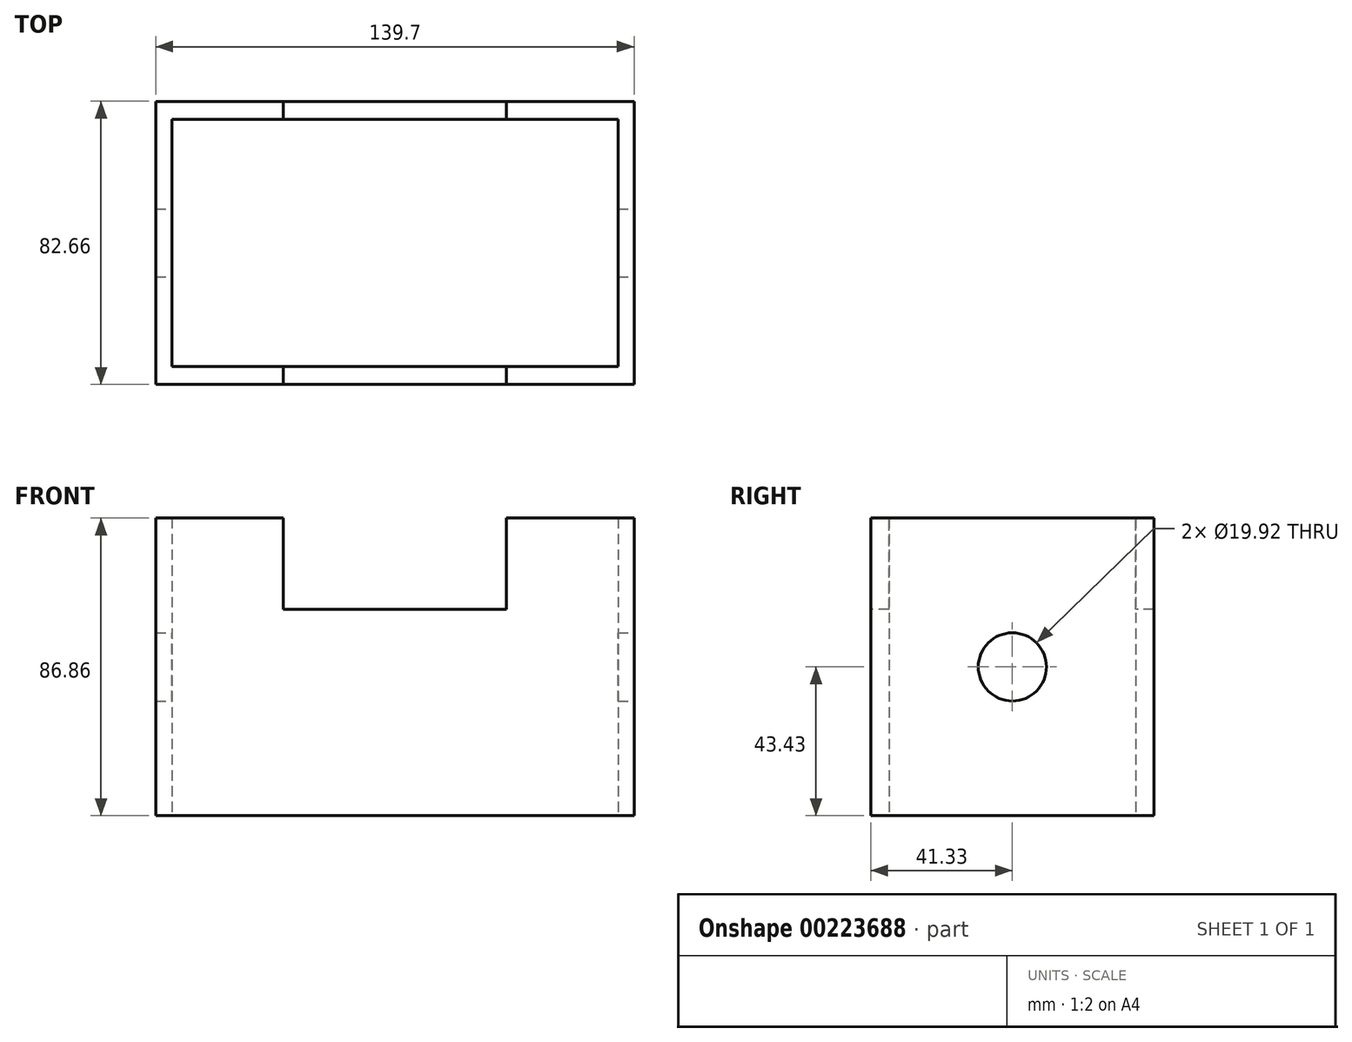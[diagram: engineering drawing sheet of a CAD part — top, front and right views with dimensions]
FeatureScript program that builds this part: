
annotation { "Feature Type Name" : "Feature", "Feature Type Description" : "" }
export const myFeature = defineFeature(function(context is Context, id is Id, definition is map)
    precondition{}
    {
        {
            var Q0;
            Q0=qCreatedBy(makeId("Top.planeOp"),FACE);
            var sketch = newSketch(context, id + "F0", { "sketchPlane" : qUnion([Q0])});
            skLineSegment(sketch, "E0.bottom", {"start": v(69.85, 41.33) * mm, "end": v(-69.85, 41.33) * mm});
            skLineSegment(sketch, "E0.top", {"start": v(69.85, -41.33) * mm, "end": v(-69.85, -41.33) * mm});
            skLineSegment(sketch, "E0.left", {"start": v(69.85, 41.33) * mm, "end": v(69.85, -41.33) * mm});
            skLineSegment(sketch, "E0.right", {"start": v(-69.85, 41.33) * mm, "end": v(-69.85, -41.33) * mm});
            skPoint(sketch, "E0.middle", {"position": v(0, 0) * mm});
            skLineSegment(sketch, "E1.bottom", {"start": v(65.12, 36.04) * mm, "end": v(-65.12, 36.04) * mm});
            skLineSegment(sketch, "E1.top", {"start": v(65.12, -36.04) * mm, "end": v(-65.12, -36.04) * mm});
            skLineSegment(sketch, "E1.left", {"start": v(65.12, 36.04) * mm, "end": v(65.12, -36.04) * mm});
            skLineSegment(sketch, "E1.right", {"start": v(-65.12, 36.04) * mm, "end": v(-65.12, -36.04) * mm});
            skSolve(sketch);
        }
        {
            var Q0;
            Q0=makeQuery(id+"F0.imprint","IMPRINT",FACE,{"disambiguationData":[TD([[makeQuery(id+"F0.imprint","IMPRINT",EDGE,{"derivedFrom":sQuery(id+"F0.wireOp",EDGE,"E0.bottom")}),1.0]])]});
            extrude(context, id + "F1", {"entities" : qUnion([Q0]), "endBound" : BoundingType.SYMMETRIC, "depth" : 86.87 * mm});
        }
        {
            var Q0;
            Q0=makeQuery(id+"F1.opExtrude","SWEPT_FACE",FACE,{"disambiguationData":[OSD([sQuery(id+"F0.wireOp",EDGE,"E0.left")])]});
            var sketch = newSketch(context, id + "F2", { "sketchPlane" : qUnion([Q0])});
            skCircle(sketch, "E2", {"center": v(0, 0) * mm, "radius": 9.96 * mm});
            skSolve(sketch);
        }
        {
            var Q0;
            Q0 = qSketchRegion(id + "F2", true);
            extrude(context, id + "F3", {"entities" : qUnion([Q0]), "operationType" : NewBodyOperationType.REMOVE, "oppositeDirection" : true, "depth" : 170.43 * mm});
        }
        {
            var Q0;
            Q0=makeQuery(id+"F1.opExtrude","SWEPT_FACE",FACE,{"disambiguationData":[OSD([sQuery(id+"F0.wireOp",EDGE,"E0.top")])]});
            var sketch = newSketch(context, id + "F4", { "sketchPlane" : qUnion([Q0])});
            skLineSegment(sketch, "E3.bottom", {"start": v(32.56, 16.84) * mm, "end": v(-32.56, 16.84) * mm});
            skLineSegment(sketch, "E3.top", {"start": v(32.56, 70.03) * mm, "end": v(-32.56, 70.03) * mm});
            skLineSegment(sketch, "E3.left", {"start": v(32.56, 16.84) * mm, "end": v(32.56, 70.03) * mm});
            skLineSegment(sketch, "E3.right", {"start": v(-32.56, 16.84) * mm, "end": v(-32.56, 70.03) * mm});
            skPoint(sketch, "E3.middle", {"position": v(0, 43.43) * mm});
            skSolve(sketch);
        }
        {
            var Q0;
            Q0 = qSketchRegion(id + "F4", true);
            extrude(context, id + "F5", {"entities" : qUnion([Q0]), "operationType" : NewBodyOperationType.REMOVE, "oppositeDirection" : true, "depth" : 111.25 * mm});
        }
    });
